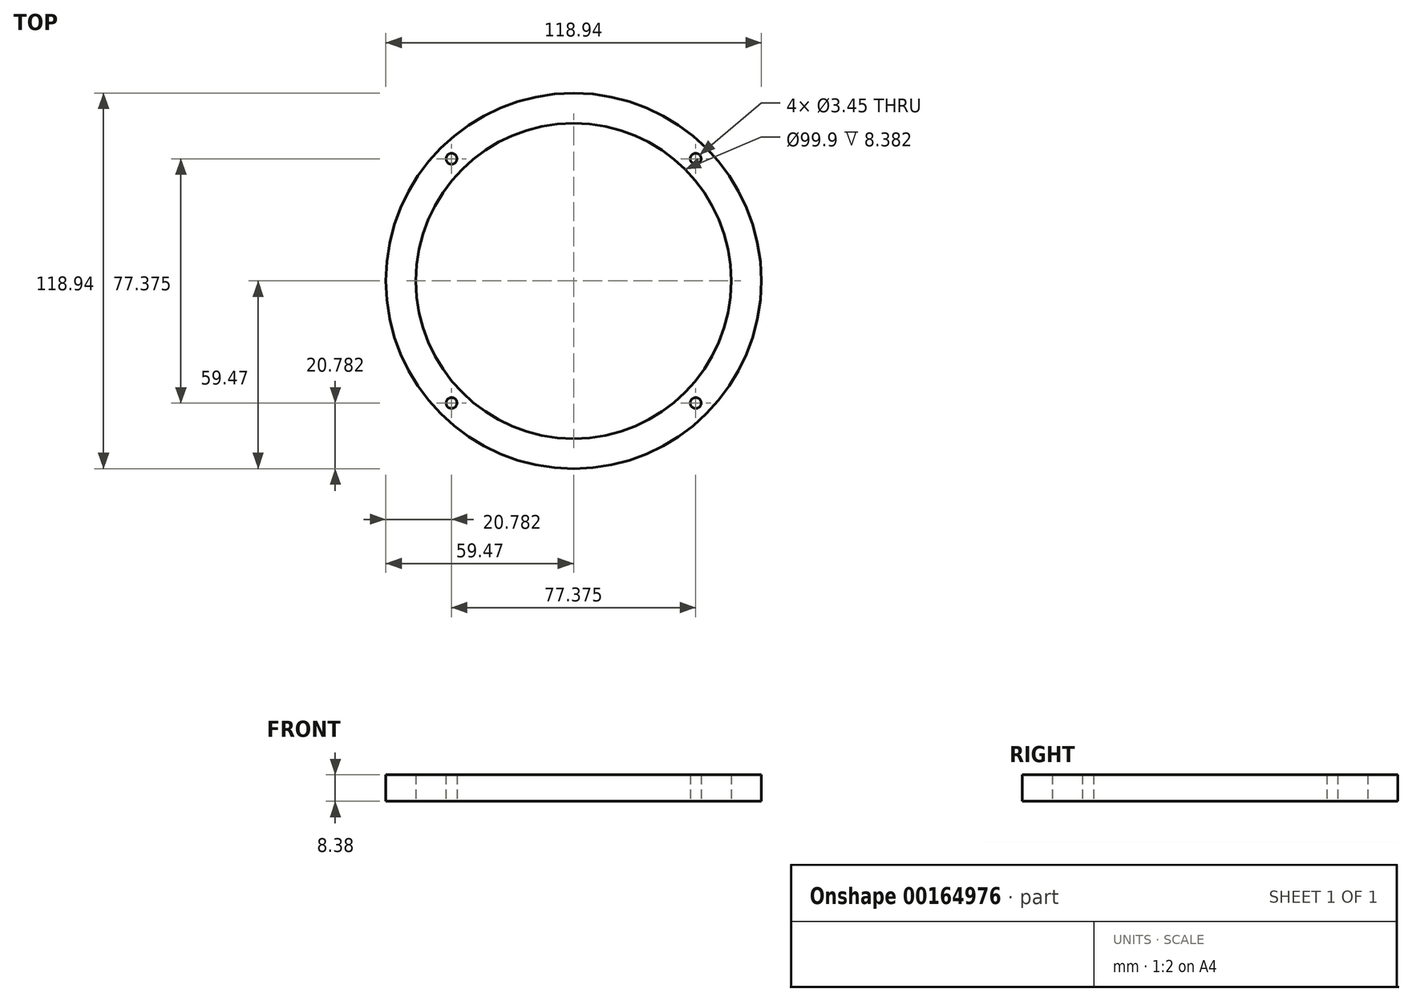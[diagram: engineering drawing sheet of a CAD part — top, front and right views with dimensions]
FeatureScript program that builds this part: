
annotation { "Feature Type Name" : "Feature", "Feature Type Description" : "" }
export const myFeature = defineFeature(function(context is Context, id is Id, definition is map)
    precondition{}
    {
        {
            var Q0;
            Q0=qCreatedBy(makeId("Top.planeOp"),FACE);
            var sketch = newSketch(context, id + "F0", { "sketchPlane" : qUnion([Q0])});
            skCircle(sketch, "E0", {"center": v(0, 0) * mm, "radius": 59.47 * mm});
            skCircle(sketch, "E1", {"center": v(0, 0) * mm, "radius": 49.95 * mm});
            skLineSegment(sketch, "E2.bottom", {"start": v(-38.69, 38.69) * mm, "end": v(38.69, 38.69) * mm, "construction": true});
            skLineSegment(sketch, "E2.top", {"start": v(-38.69, -38.69) * mm, "end": v(38.69, -38.69) * mm, "construction": true});
            skLineSegment(sketch, "E2.left", {"start": v(-38.69, 38.69) * mm, "end": v(-38.69, -38.69) * mm, "construction": true});
            skLineSegment(sketch, "E2.right", {"start": v(38.69, 38.69) * mm, "end": v(38.69, -38.69) * mm, "construction": true});
            skCircle(sketch, "E3", {"center": v(-38.69, 38.69) * mm, "radius": 4.76 * mm, "construction": true});
            skCircle(sketch, "E4", {"center": v(-38.69, 38.69) * mm, "radius": 1.73 * mm});
            skCircle(sketch, "E5", {"center": v(38.69, 38.69) * mm, "radius": 1.73 * mm});
            skCircle(sketch, "E6", {"center": v(38.69, -38.69) * mm, "radius": 1.73 * mm});
            skCircle(sketch, "E7", {"center": v(-38.69, -38.69) * mm, "radius": 1.73 * mm});
            skSolve(sketch);
        }
        {
            var Q0;
            Q0=qSketchRegion(id+"F0",true);
            extrude(context, id + "F1", {"entities" : qUnion([Q0]), "depth" : 8.38 * mm});
        }
    });
